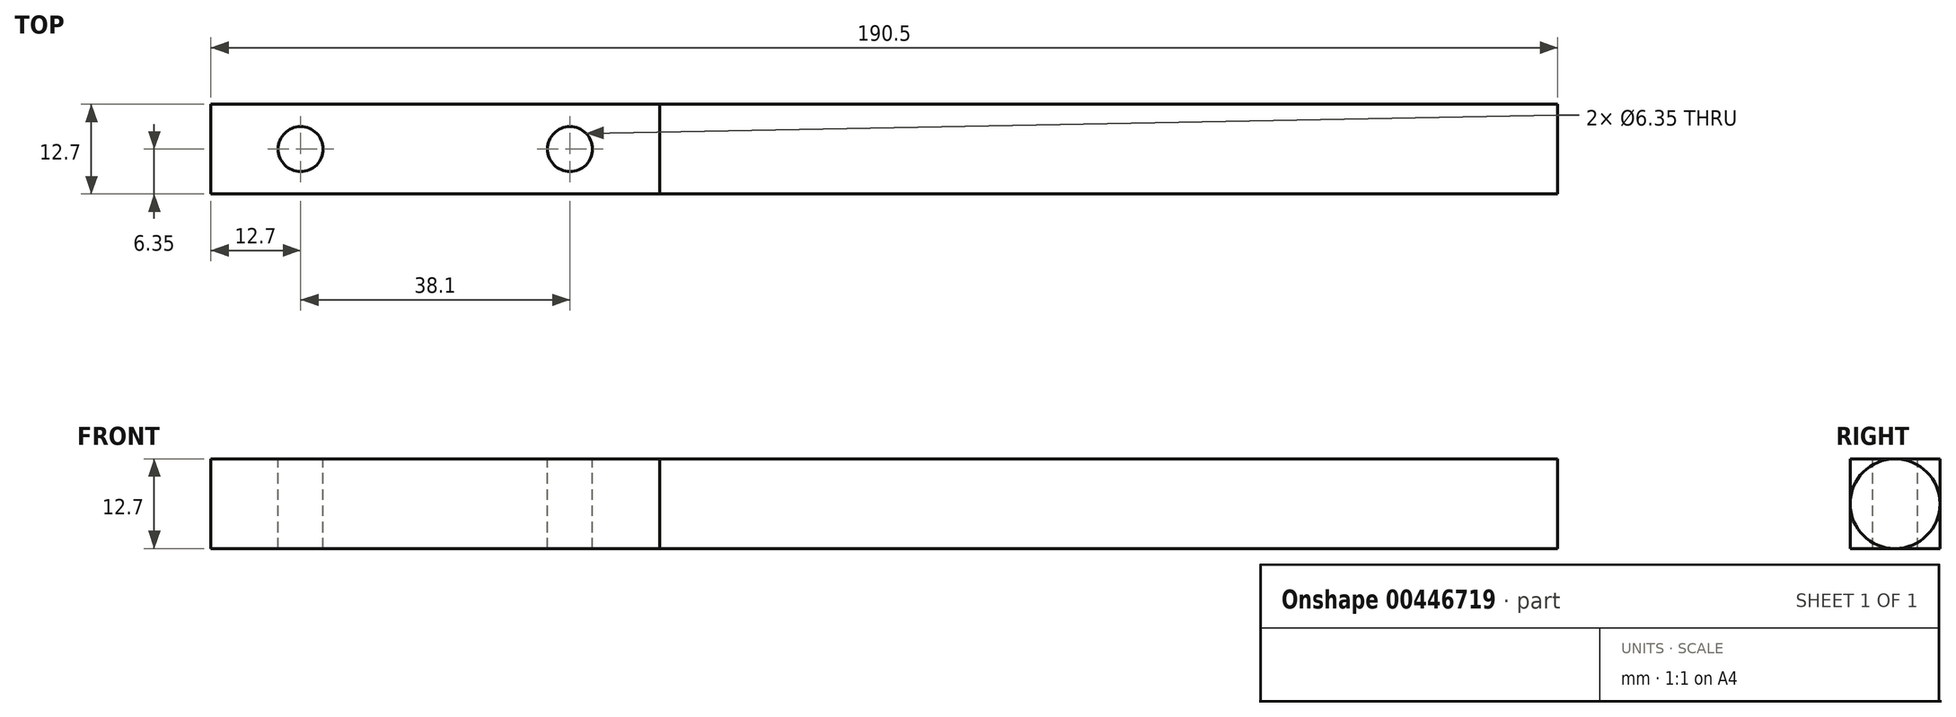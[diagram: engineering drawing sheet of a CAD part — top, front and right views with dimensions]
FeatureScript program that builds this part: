
annotation { "Feature Type Name" : "Feature", "Feature Type Description" : "" }
export const myFeature = defineFeature(function(context is Context, id is Id, definition is map)
    precondition{}
    {
        {
            var Q0;
            Q0=qCreatedBy(makeId("Top.planeOp"),FACE);
            var sketch = newSketch(context, id + "F0", { "sketchPlane" : qUnion([Q0])});
            skLineSegment(sketch, "E0.bottom", {"start": v(0, 6.35) * mm, "end": v(-63.5, 6.35) * mm});
            skLineSegment(sketch, "E0.top", {"start": v(0, -6.35) * mm, "end": v(-63.5, -6.35) * mm});
            skLineSegment(sketch, "E0.left", {"start": v(0, 6.35) * mm, "end": v(0, -6.35) * mm});
            skLineSegment(sketch, "E0.right", {"start": v(-63.5, 6.35) * mm, "end": v(-63.5, -6.35) * mm});
            skCircle(sketch, "E1", {"center": v(-50.8, 0) * mm, "radius": 3.18 * mm});
            skCircle(sketch, "E2", {"center": v(-12.7, 0) * mm, "radius": 3.18 * mm});
            skSolve(sketch);
        }
        {
            var Q0;
            Q0=makeQuery(id+"F0.imprint","IMPRINT",FACE,{"disambiguationData":[TD([[makeQuery(id+"F0.imprint","IMPRINT",EDGE,{"derivedFrom":sQuery(id+"F0.wireOp",EDGE,"E0.bottom")}),1.0]])]});
            extrude(context, id + "F1", {"entities" : qUnion([Q0]), "endBound" : BoundingType.SYMMETRIC, "oppositeDirection" : true, "depth" : 12.7 * mm});
        }
        {
            var Q0;
            Q0=qCreatedBy(makeId("Top.planeOp"),FACE);
            var sketch = newSketch(context, id + "F2", { "sketchPlane" : qUnion([Q0])});
            skLineSegment(sketch, "E3.bottom", {"start": v(0, 0) * mm, "end": v(127, 0) * mm});
            skLineSegment(sketch, "E3.top", {"start": v(0, 6.35) * mm, "end": v(127, 6.35) * mm});
            skLineSegment(sketch, "E3.left", {"start": v(0, 0) * mm, "end": v(0, 6.35) * mm});
            skLineSegment(sketch, "E3.right", {"start": v(127, 0) * mm, "end": v(127, 6.35) * mm});
            skSolve(sketch);
        }
        {
            var Q0;
            Q0=makeQuery(id+"F2.imprint","IMPRINT",FACE,{"disambiguationData":[TD([[makeQuery(id+"F2.imprint","IMPRINT",EDGE,{"derivedFrom":sQuery(id+"F2.wireOp",EDGE,"E3.bottom")}),1.0]])]});
            var Q1;
            Q1=sQuery(id+"F2.wireOp",EDGE,"E3.bottom");
            revolve(context, id + "F3", {"operationType" : NewBodyOperationType.ADD, "entities" : qUnion([Q0]), "axis" : qUnion([Q1]), "revolveType" : RevolveType.FULL});
        }
    });
